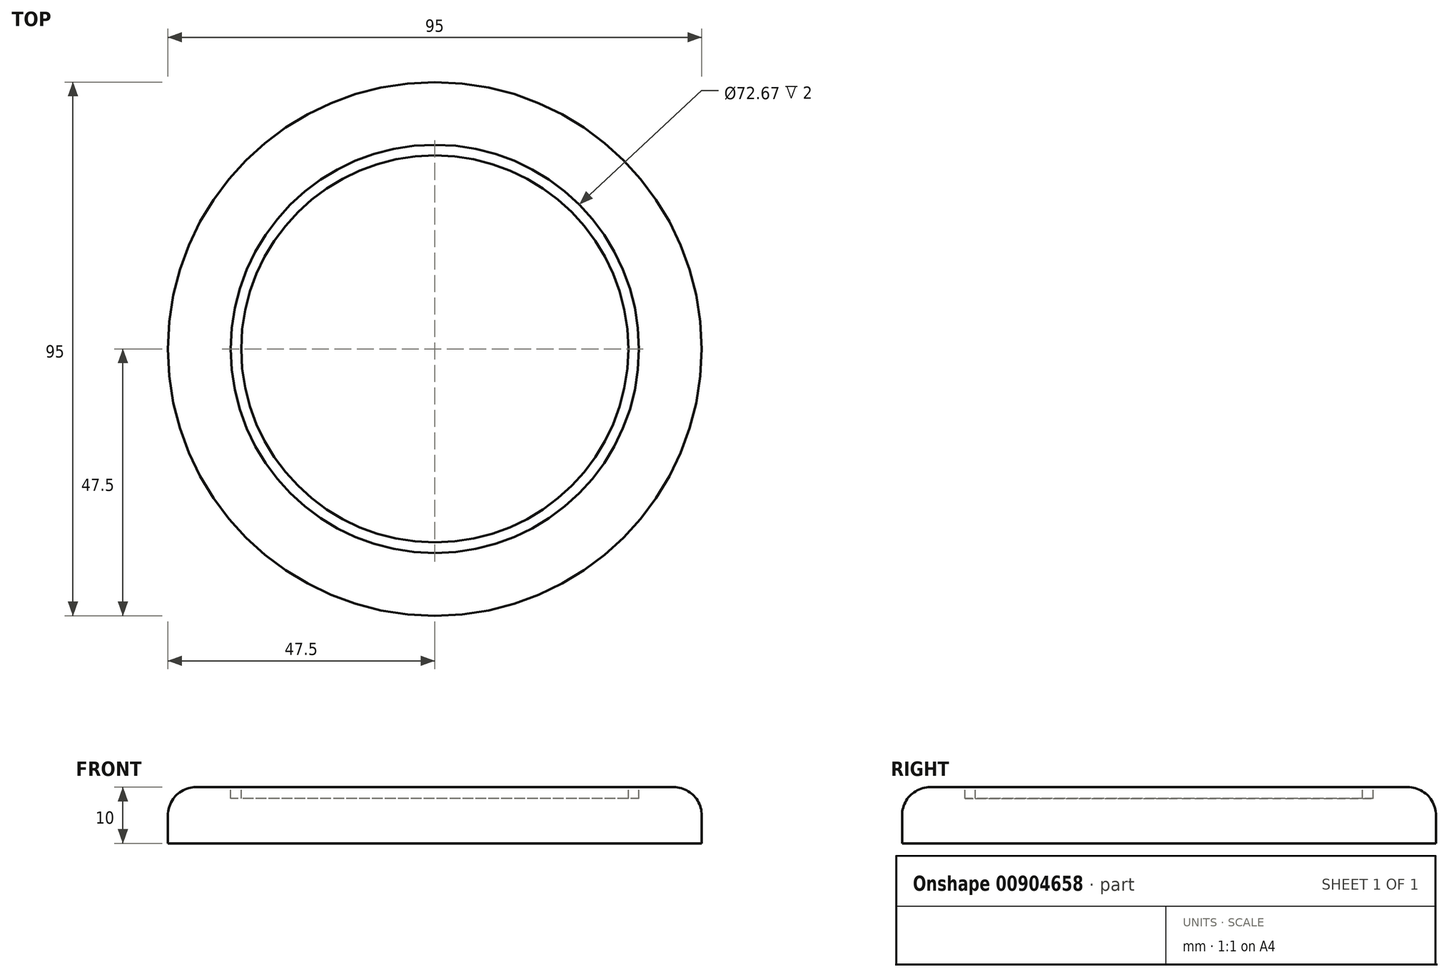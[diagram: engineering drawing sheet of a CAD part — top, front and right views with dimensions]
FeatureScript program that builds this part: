
annotation { "Feature Type Name" : "Feature", "Feature Type Description" : "" }
export const myFeature = defineFeature(function(context is Context, id is Id, definition is map)
    precondition{}
    {
        {
            var Q0;
            Q0=qCreatedBy(makeId("Top.planeOp"),FACE);
            var sketch = newSketch(context, id + "F0", { "sketchPlane" : qUnion([Q0])});
            skCircle(sketch, "E0", {"center": v(0, 0) * mm, "radius": 47.5 * mm});
            skSolve(sketch);
        }
        {
            var Q0;
            Q0=makeQuery(id+"F0.imprint","IMPRINT",FACE,{"disambiguationData":[TD([[makeQuery(id+"F0.imprint","IMPRINT",EDGE,{"derivedFrom":sQuery(id+"F0.wireOp",EDGE,"E0")}),1.0]])]});
            extrude(context, id + "F1", {"entities" : qUnion([Q0]), "depth" : 10 * mm, "offsetDistance" : 25 * mm});
        }
        {
            var Q0;
            Q0=makeQuery(id+"F1.opExtrude","CAP_EDGE",EDGE,{"disambiguationData":[OSD([sQuery(id+"F0.wireOp",EDGE,"E0")])],"isStart":false});
            fillet(context, id + "F2", {"entities" : qUnion([Q0]), "radius" : 5 * mm, "tangentPropagation" : true, "allowEdgeOverflow" : false});
        }
        {
            var Q0;
            Q0=makeQuery(id+"F1.opExtrude","CAP_FACE",FACE,{"disambiguationData":[OSD([sQuery(id+"F0.wireOp",EDGE,"E0")])],"isStart":false});
            var sketch = newSketch(context, id + "F3", { "sketchPlane" : qUnion([Q0])});
            skCircle(sketch, "E1", {"center": v(0, 0) * mm, "radius": 36.34 * mm});
            skCircle(sketch, "E2", {"center": v(0, 0) * mm, "radius": 34.44 * mm});
            skSolve(sketch);
        }
        {
            var Q0;
            Q0 = qSketchRegion(id + "F3", true);
            extrude(context, id + "F4", {"entities" : qUnion([Q0]), "operationType" : NewBodyOperationType.REMOVE, "oppositeDirection" : true, "depth" : 2 * mm, "offsetDistance" : 25 * mm});
        }
    });
